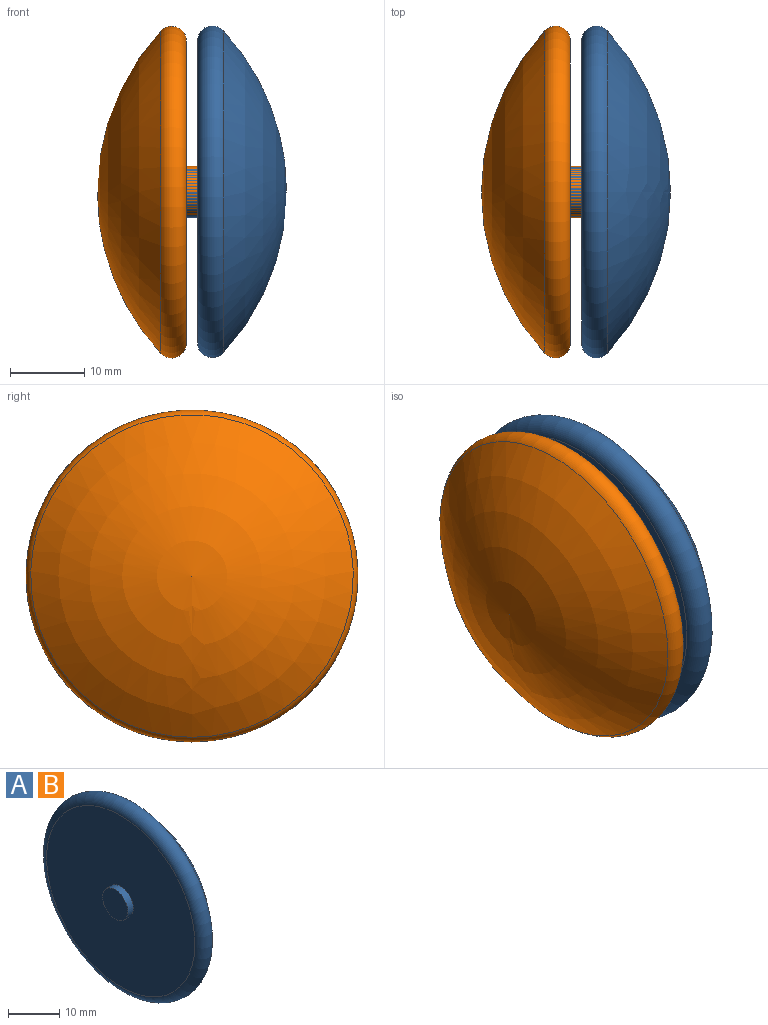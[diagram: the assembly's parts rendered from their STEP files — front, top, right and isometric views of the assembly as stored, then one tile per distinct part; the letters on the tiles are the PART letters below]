
ASSEMBLY  parts=2 mates=1
PART A: 5 faces, bbox 13.5x48.5x48.5 mm
  f0: plane 40.84x40.84mm, normal (-1,0,0), area 1271.4mm2, adj f2,f4
  f1: sphere r=32.02mm, area 1719.9mm2, adj f4
  f2: cylinder r=3.5mm len=7mm, axis (1,0,0), area 33mm2, adj f0,f3
  f3: plane 7x7mm, normal (-1,0,0), area 38.5mm2, adj f2
  f4: torus R=20.42mm, axis (-1,0,0), area 657.7mm2, adj f0,f1
PART B: same geometry as A
PLACE A t=(-30.55,29.9,-22.59)mm
PLACE B rot(axis=(0,1,0),180deg) t=(-32.05,29.9,27.41)mm
MATE fastened B.f2 <-> A.f2  axis (1,0,0) through (-32.05,29.9,2.41)mm
